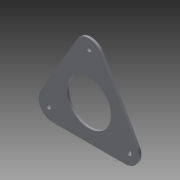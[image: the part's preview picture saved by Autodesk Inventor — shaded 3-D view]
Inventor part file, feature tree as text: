
AUTODESK INVENTOR PART (.ipt)
format: ipt  version: 2013 (Build 170138000, 138)  size: 95,232 bytes
history: native  units: in
note: dims shown in document units (in); Inventor stores cm internally (conversion verified against a paired STEP export)
features: extrude x1, fillet x1, sketch x1
ambient origin geometry x8: Origin, YZ Plane, XZ Plane, XY Plane, X Axis, Y Axis, Z Axis, Center Point
bodies: Solid1 (feature_tree)
feature tree (3):
  extrude  "Extrusion1"  Depth=0.25in
  fillet  "Fillet1"  Radius=2.5in
  sketch  "Sketch2"  dims[d0=2.37in d1=0.25in d2=2.5in d3=1.1811in d5=360.0deg d8=0.5in d9=0.5in d10=0.5in d11=0.125in d12=0.0in d13=0.75in]
